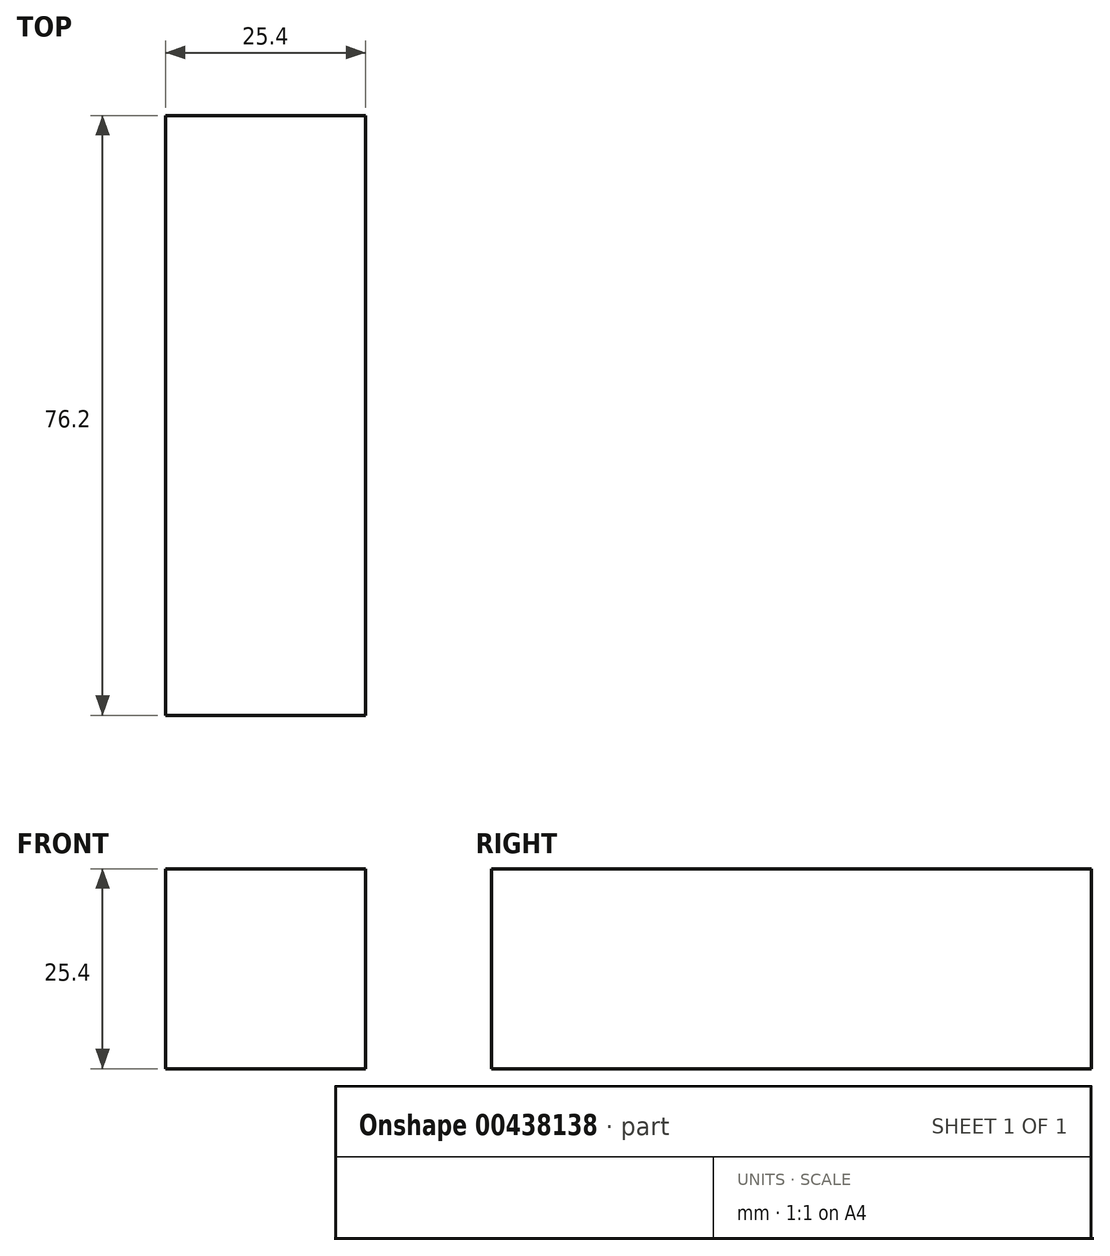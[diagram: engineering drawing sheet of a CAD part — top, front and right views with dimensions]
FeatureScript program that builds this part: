
annotation { "Feature Type Name" : "Feature", "Feature Type Description" : "" }
export const myFeature = defineFeature(function(context is Context, id is Id, definition is map)
    precondition{}
    {
        {
            var Q0;
            Q0=qCreatedBy(makeId("Front.planeOp"),FACE);
            var sketch = newSketch(context, id + "F0", { "sketchPlane" : qUnion([Q0])});
            skLineSegment(sketch, "E0.bottom", {"start": v(-14.13, 29.8) * mm, "end": v(11.27, 29.8) * mm});
            skLineSegment(sketch, "E0.top", {"start": v(-14.13, 4.4) * mm, "end": v(11.27, 4.4) * mm});
            skLineSegment(sketch, "E0.left", {"start": v(-14.13, 29.8) * mm, "end": v(-14.13, 4.4) * mm});
            skLineSegment(sketch, "E0.right", {"start": v(11.27, 29.8) * mm, "end": v(11.27, 4.4) * mm});
            skSolve(sketch);
        }
        {
            var Q0;
            Q0=makeQuery(id+"F0.imprint","IMPRINT",FACE,{"disambiguationData":[TD([[makeQuery(id+"F0.imprint","IMPRINT",EDGE,{"derivedFrom":sQuery(id+"F0.wireOp",EDGE,"E0.bottom")}),-1.0]])]});
            extrude(context, id + "F1", {"entities" : qUnion([Q0]), "depth" : 76.2 * mm});
        }
    });
